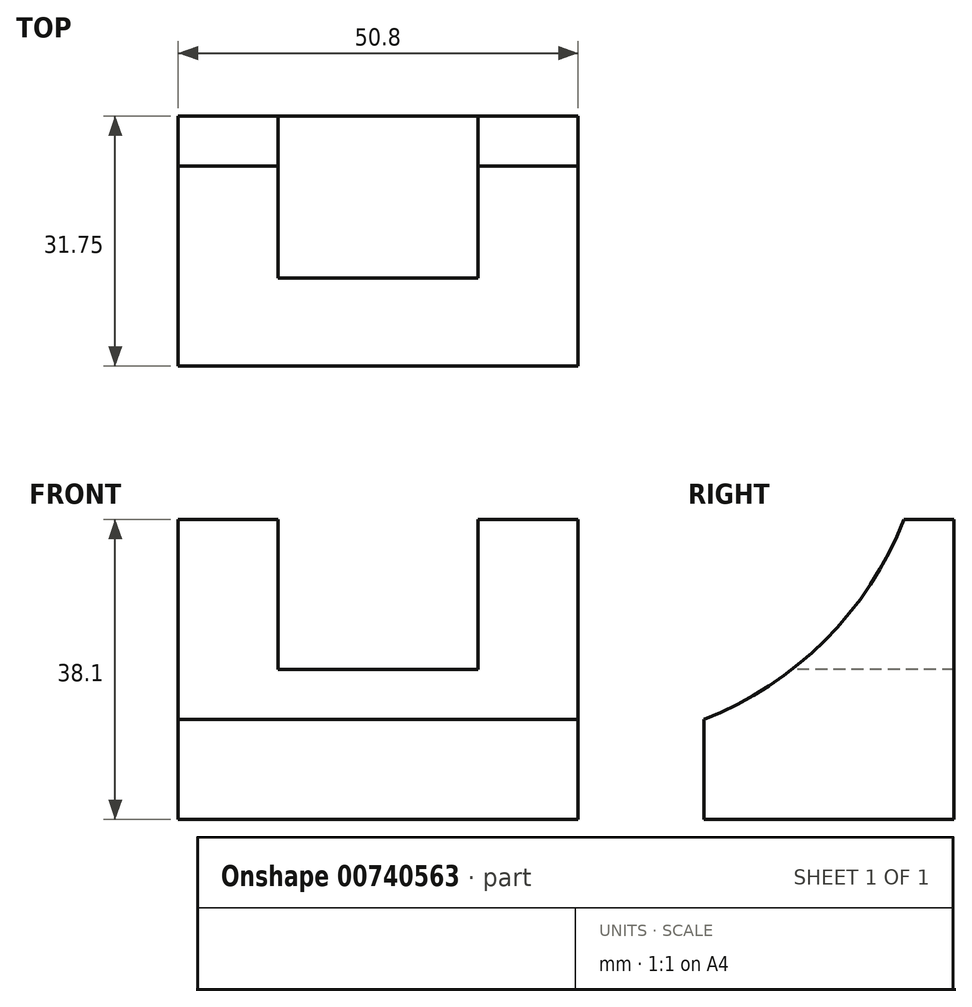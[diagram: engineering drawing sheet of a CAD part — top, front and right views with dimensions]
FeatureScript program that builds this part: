
annotation { "Feature Type Name" : "Feature", "Feature Type Description" : "" }
export const myFeature = defineFeature(function(context is Context, id is Id, definition is map)
    precondition{}
    {
        {
            var Q0;
            Q0=qCreatedBy(makeId("Front.planeOp"),FACE);
            var sketch = newSketch(context, id + "F0", { "sketchPlane" : qUnion([Q0])});
            skLineSegment(sketch, "E0", {"start": v(0, 0) * mm, "end": v(50.8, 0) * mm});
            skLineSegment(sketch, "E1", {"start": v(50.8, 0) * mm, "end": v(50.8, 38.1) * mm});
            skLineSegment(sketch, "E2", {"start": v(50.8, 38.1) * mm, "end": v(0, 38.1) * mm});
            skLineSegment(sketch, "E3", {"start": v(0, 38.1) * mm, "end": v(0, 0) * mm});
            skSolve(sketch);
        }
        {
            var Q0;
            Q0 = qSketchRegion(id + "F0", true);
            extrude(context, id + "F1", {"entities" : qUnion([Q0]), "depth" : 31.75 * mm, "offsetDistance" : 25.4 * mm});
        }
        {
            var Q0;
            Q0=makeQuery(id+"F1.opExtrude","CAP_FACE",FACE,{"disambiguationData":[OSD([sQuery(id+"F0.wireOp",EDGE,"E0"),sQuery(id+"F0.wireOp",EDGE,"E1"),sQuery(id+"F0.wireOp",EDGE,"E2"),sQuery(id+"F0.wireOp",EDGE,"E3")])],"isStart":false});
            var sketch = newSketch(context, id + "F2", { "sketchPlane" : qUnion([Q0])});
            skLineSegment(sketch, "E4", {"start": v(12.7, 38.1) * mm, "end": v(12.7, 19.05) * mm});
            skLineSegment(sketch, "E5", {"start": v(12.7, 19.05) * mm, "end": v(38.1, 19.05) * mm});
            skLineSegment(sketch, "E6", {"start": v(38.1, 19.05) * mm, "end": v(38.1, 38.1) * mm});
            skSolve(sketch);
        }
        {
            var Q0;
            Q0 = qSketchRegion(id + "F2", true);
            var Q1;
            {var subQ0=sQuery(id+"F2.wireOp",EDGE,"E4");Q1=makeQuery(id+"F2.imprint","IMPRINT",FACE,{"disambiguationData":[TD([[makeQuery(id+"F2.imprint","IMPRINT",EDGE,{"derivedFrom":subQ0}),1.0]])]});}
            extrude(context, id + "F3", {"entities" : qUnion([Q0, Q1]), "operationType" : NewBodyOperationType.REMOVE, "endBound" : BoundingType.THROUGH_ALL, "oppositeDirection" : true, "depth" : 25.4 * mm, "offsetDistance" : 25.4 * mm});
        }
        {
            var Q0;
            Q0=makeQuery(id+"F1.opExtrude","SWEPT_FACE",FACE,{"disambiguationData":[OSD([sQuery(id+"F0.wireOp",EDGE,"E1")])]});
            var sketch = newSketch(context, id + "F4", { "sketchPlane" : qUnion([Q0])});
            skArc(sketch, "E7", {"start": v(-31.75, 12.7) * mm, "mid": v(-16.4, 22.75) * mm, "end": v(-6.35, 38.1) * mm});
            skSolve(sketch);
        }
        {
            var Q0;
            {var subQ0=sQuery(id+"F4.wireOp",EDGE,"E7");Q0=makeQuery(id+"F4.imprint","IMPRINT",FACE,{"disambiguationData":[TD([[makeQuery(id+"F4.imprint","IMPRINT",EDGE,{"derivedFrom":subQ0}),1.0]])]});}
            extrude(context, id + "F5", {"entities" : qUnion([Q0]), "operationType" : NewBodyOperationType.REMOVE, "endBound" : BoundingType.THROUGH_ALL, "oppositeDirection" : true, "depth" : 25.4 * mm, "offsetDistance" : 25.4 * mm});
        }
    });
